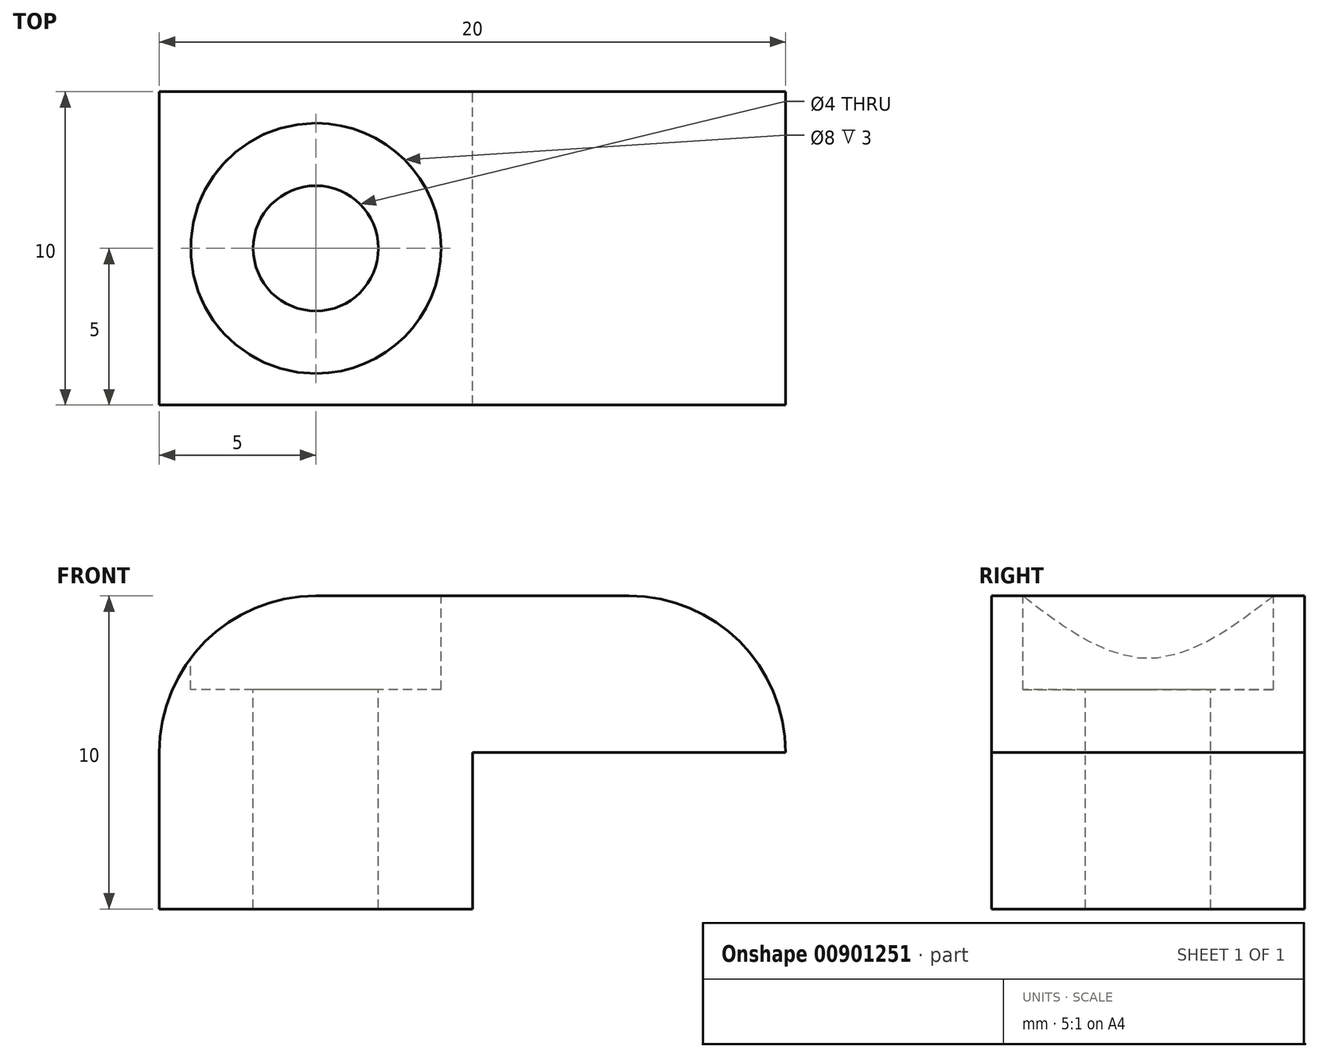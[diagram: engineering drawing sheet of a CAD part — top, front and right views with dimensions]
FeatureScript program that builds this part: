
annotation { "Feature Type Name" : "Feature", "Feature Type Description" : "" }
export const myFeature = defineFeature(function(context is Context, id is Id, definition is map)
    precondition{}
    {
        {
            var Q0;
            Q0=qCreatedBy(makeId("Front.planeOp"),FACE);
            var sketch = newSketch(context, id + "F0", { "sketchPlane" : qUnion([Q0])});
            skLineSegment(sketch, "E0", {"start": v(0, 0) * mm, "end": v(10, 0) * mm});
            skLineSegment(sketch, "E1", {"start": v(10, 0) * mm, "end": v(10, 5) * mm});
            skLineSegment(sketch, "E2", {"start": v(10, 5) * mm, "end": v(20, 5) * mm});
            skLineSegment(sketch, "E3", {"start": v(20, 5) * mm, "end": v(20, 10) * mm});
            skLineSegment(sketch, "E4", {"start": v(20, 10) * mm, "end": v(0, 10) * mm});
            skLineSegment(sketch, "E5", {"start": v(0, 10) * mm, "end": v(0, 0) * mm});
            skSolve(sketch);
        }
        {
            var Q0;
            Q0 = qSketchRegion(id + "F0", true);
            extrude(context, id + "F1", {"entities" : qUnion([Q0]), "depth" : 10 * mm, "offsetDistance" : 25 * mm});
        }
        {
            var Q0;
            Q0=makeQuery(id+"F1.opExtrude","SWEPT_EDGE",EDGE,{"disambiguationData":[OSD([sQuery(id+"F0.wireOp",EDGE,"E3"),sQuery(id+"F0.wireOp",EDGE,"E4")])]});
            var Q1;
            Q1=makeQuery(id+"F1.opExtrude","SWEPT_EDGE",EDGE,{"disambiguationData":[OSD([sQuery(id+"F0.wireOp",EDGE,"E4"),sQuery(id+"F0.wireOp",EDGE,"E5")])]});
            fillet(context, id + "F2", {"entities" : qUnion([Q0, Q1]), "radius" : 5 * mm, "tangentPropagation" : true, "allowEdgeOverflow" : false});
        }
        {
            var Q0;
            Q0=makeQuery(id+"F1.opExtrude","SWEPT_FACE",FACE,{"disambiguationData":[OSD([sQuery(id+"F0.wireOp",EDGE,"E4")])]});
            var sketch = newSketch(context, id + "F3", { "sketchPlane" : qUnion([Q0])});
            skCircle(sketch, "E6", {"center": v(5, -5) * mm, "radius": 2 * mm});
            skSolve(sketch);
        }
        {
            var Q0;
            Q0 = qSketchRegion(id + "F3", true);
            extrude(context, id + "F4", {"entities" : qUnion([Q0]), "operationType" : NewBodyOperationType.REMOVE, "oppositeDirection" : true, "depth" : 25 * mm, "offsetDistance" : 25 * mm});
        }
        {
            var Q0;
            Q0=makeQuery(id+"F1.opExtrude","SWEPT_FACE",FACE,{"disambiguationData":[OSD([sQuery(id+"F0.wireOp",EDGE,"E4")])]});
            var sketch = newSketch(context, id + "F5", { "sketchPlane" : qUnion([Q0])});
            skCircle(sketch, "E7", {"center": v(5, -5) * mm, "radius": 4 * mm});
            skSolve(sketch);
        }
        {
            var Q0;
            Q0 = qSketchRegion(id + "F5", true);
            extrude(context, id + "F6", {"entities" : qUnion([Q0]), "operationType" : NewBodyOperationType.REMOVE, "oppositeDirection" : true, "depth" : 3 * mm, "offsetDistance" : 25 * mm});
        }
    });
